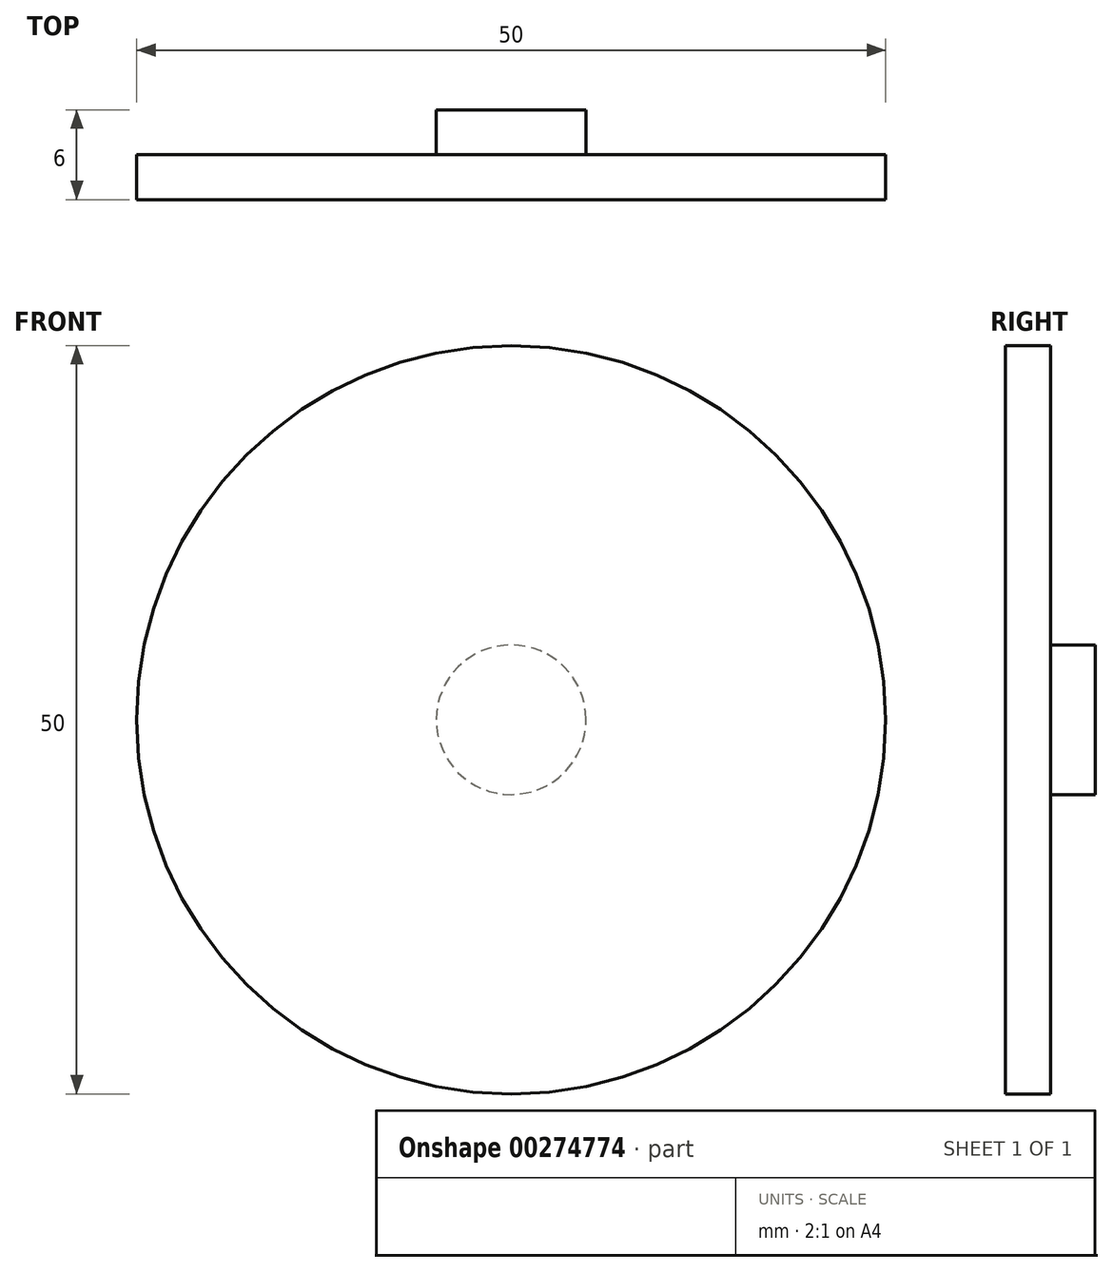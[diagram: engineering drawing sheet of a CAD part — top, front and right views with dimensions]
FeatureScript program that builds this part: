
annotation { "Feature Type Name" : "Feature", "Feature Type Description" : "" }
export const myFeature = defineFeature(function(context is Context, id is Id, definition is map)
    precondition{}
    {
        {
            var Q0;
            Q0=qCreatedBy(makeId("Front.planeOp"),FACE);
            var sketch = newSketch(context, id + "F0", { "sketchPlane" : qUnion([Q0])});
            skCircle(sketch, "E0", {"center": v(0, 0) * mm, "radius": 25 * mm});
            skCircle(sketch, "E1", {"center": v(0, 0) * mm, "radius": 5 * mm});
            skSolve(sketch);
        }
        {
            var Q0;
            Q0 = qSketchRegion(id + "F0", true);
            var Q1;
            Q1=makeQuery(id+"F0.imprint","IMPRINT",FACE,{"disambiguationData":[TD([[makeQuery(id+"F0.imprint","IMPRINT",EDGE,{"derivedFrom":sQuery(id+"F0.wireOp",EDGE,"E1")}),1.0]])]});
            extrude(context, id + "F1", {"entities" : qUnion([Q0, Q1]), "depth" : 3 * mm});
        }
        {
            var Q0;
            Q0=makeQuery(id+"F0.imprint","IMPRINT",FACE,{"disambiguationData":[TD([[makeQuery(id+"F0.imprint","IMPRINT",EDGE,{"derivedFrom":sQuery(id+"F0.wireOp",EDGE,"E1")}),1.0]])]});
            extrude(context, id + "F2", {"entities" : qUnion([Q0]), "operationType" : NewBodyOperationType.ADD, "oppositeDirection" : true, "depth" : 3 * mm});
        }
    });
